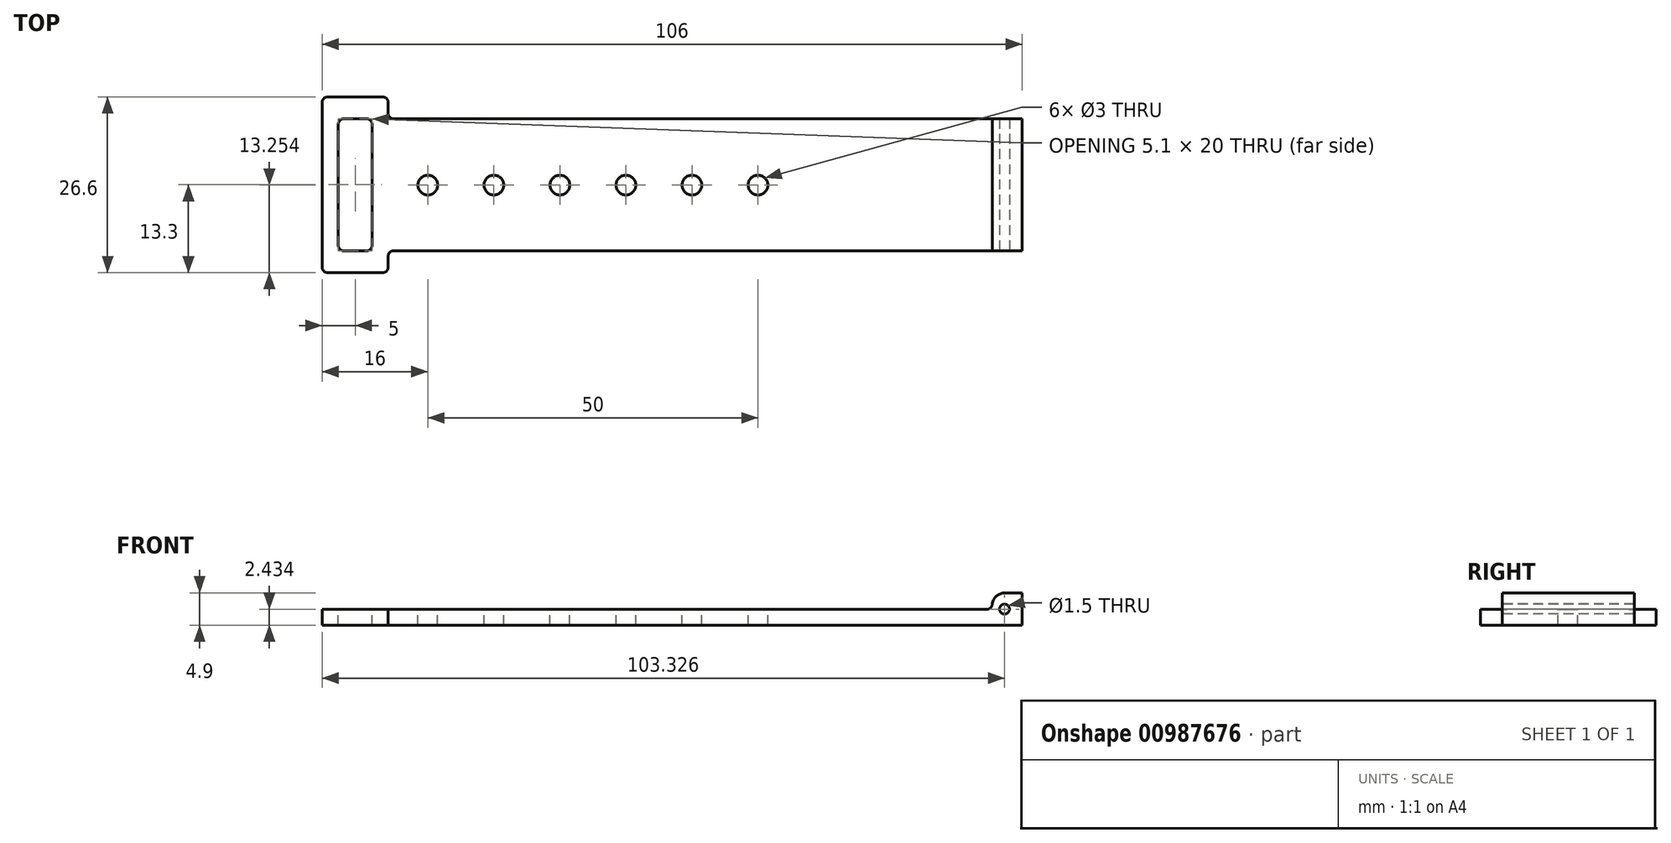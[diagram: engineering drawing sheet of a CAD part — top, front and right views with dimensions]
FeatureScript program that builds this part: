
annotation { "Feature Type Name" : "Feature", "Feature Type Description" : "" }
export const myFeature = defineFeature(function(context is Context, id is Id, definition is map)
    precondition{}
    {
        {
            var Q0;
            Q0=qCreatedBy(makeId("Top.planeOp"),FACE);
            var sketch = newSketch(context, id + "F0", { "sketchPlane" : qUnion([Q0])});
            skLineSegment(sketch, "E0", {"start": v(0, 0) * mm, "end": v(-96, 0) * mm});
            skLineSegment(sketch, "E1", {"start": v(-96, 20) * mm, "end": v(0, 20) * mm});
            skLineSegment(sketch, "E2", {"start": v(0, 20) * mm, "end": v(0, 0) * mm});
            skPoint(sketch, "E3.visualSharp", {"position": v(-100, 20) * mm});
            skPoint(sketch, "E4.visualSharp", {"position": v(-100, 0) * mm});
            skLineSegment(sketch, "E5", {"start": v(-96, 20) * mm, "end": v(-96, 0) * mm});
            skSolve(sketch);
        }
        {
            var Q0;
            Q0=makeQuery(id+"F0.imprint","IMPRINT",FACE,{"disambiguationData":[TD([[makeQuery(id+"F0.imprint","IMPRINT",EDGE,{"derivedFrom":sQuery(id+"F0.wireOp",EDGE,"E0")}),-1.0]])]});
            extrude(context, id + "F1", {"entities" : qUnion([Q0]), "depth" : 2.4 * mm, "offsetDistance" : 25 * mm});
        }
        {
            var Q0;
            Q0=makeQuery(id+"F1.opExtrude","CAP_FACE",FACE,{"disambiguationData":[OSD([sQuery(id+"F0.wireOp",EDGE,"E0"),sQuery(id+"F0.wireOp",EDGE,"AKXXqW1o-zOXN-sCXT-5YLg-LlBWR1qxFu5Y"),sQuery(id+"F0.wireOp",EDGE,"E1"),sQuery(id+"F0.wireOp",EDGE,"E2"),sQuery(id+"F0.wireOp",EDGE,"E3.filletArc"),sQuery(id+"F0.wireOp",EDGE,"E4.filletArc")])],"isStart":false});
            var sketch = newSketch(context, id + "F2", { "sketchPlane" : qUnion([Q0])});
            skLineSegment(sketch, "E6", {"start": v(0, 20) * mm, "end": v(-4, 20) * mm});
            skLineSegment(sketch, "E7", {"start": v(-4, 20) * mm, "end": v(-4, 0) * mm});
            skLineSegment(sketch, "E8", {"start": v(-4, 0) * mm, "end": v(0, 0) * mm});
            skLineSegment(sketch, "E9", {"start": v(0, 0) * mm, "end": v(0, 20) * mm});
            skLineSegment(sketch, "E10", {"start": v(-96, 20) * mm, "end": v(0, 0) * mm});
            skSolve(sketch);
        }
        {
            var Q0;
            Q0=makeQuery(id+"F1.opExtrude","SWEPT_FACE",FACE,{"disambiguationData":[OSD([sQuery(id+"F0.wireOp",EDGE,"E0")])]});
            var sketch = newSketch(context, id + "F3", { "sketchPlane" : qUnion([Q0])});
            skLineSegment(sketch, "E11", {"start": v(0, 2.4) * mm, "end": v(0, 4.9) * mm});
            skLineSegment(sketch, "E12", {"start": v(0, 4.9) * mm, "end": v(-2.56, 4.9) * mm});
            skLineSegment(sketch, "E13", {"start": v(-4.54, 2.4) * mm, "end": v(0, 2.4) * mm});
            skPoint(sketch, "E14.visualSharp", {"position": v(-4.54, 4.9) * mm});
            skArc(sketch, "E14.filletArc", {"start": v(-2.56, 4.9) * mm, "mid": v(-3.86, 4.42) * mm, "end": v(-4.54, 3.2) * mm});
            skLineSegment(sketch, "E15", {"start": v(-5.34, 2.4) * mm, "end": v(-5.73, 2.4) * mm});
            skPoint(sketch, "E16.visualSharp", {"position": v(-4.54, 2.4) * mm});
            skArc(sketch, "E16.filletArc", {"start": v(-5.34, 2.4) * mm, "mid": v(-4.77, 2.63) * mm, "end": v(-4.54, 3.2) * mm});
            skSolve(sketch);
        }
        {
            var Q0;
            Q0=makeQuery(id+"F3.imprint","IMPRINT",FACE,{"disambiguationData":[TD([[makeQuery(id+"F3.imprint","IMPRINT",EDGE,{"derivedFrom":sQuery(id+"F3.wireOp",EDGE,"E11")}),1.0]])]});
            extrude(context, id + "F4", {"entities" : qUnion([Q0]), "operationType" : NewBodyOperationType.ADD, "oppositeDirection" : true, "depth" : 20 * mm, "offsetDistance" : 25 * mm});
        }
        {
            var Q0;
            Q0=makeQuery(id+"F4.boolean.opBoolean","MERGE",FACE,{"derivedFrom":[makeQuery(id+"F1.opExtrude","SWEPT_FACE",FACE,{"disambiguationData":[OSD([sQuery(id+"F0.wireOp",EDGE,"E0")])]}),makeQuery(id+"F4.opExtrude","CAP_FACE",FACE,{"disambiguationData":[OSD([sQuery(id+"F3.wireOp",EDGE,"E11"),sQuery(id+"F3.wireOp",EDGE,"E12"),sQuery(id+"F3.wireOp",EDGE,"nSELvPSm-3Vxk-T1EU-R1aP-sd0dZwsSSjfP"),sQuery(id+"F3.wireOp",EDGE,"E14.filletArc"),sQuery(id+"F3.wireOp",EDGE,"E13")])],"isStart":true})]});
            var sketch = newSketch(context, id + "F5", { "sketchPlane" : qUnion([Q0])});
            skCircle(sketch, "E17", {"center": v(-2.67, 2.43) * mm, "radius": 0.75 * mm});
            skLineSegment(sketch, "E18", {"start": v(0, 4.9) * mm, "end": v(0, 2.43) * mm});
            skLineSegment(sketch, "E19", {"start": v(0, 2.43) * mm, "end": v(-2.67, 2.43) * mm});
            skSolve(sketch);
        }
        {
            var Q0;
            Q0=makeQuery(id+"F5.imprint","IMPRINT",FACE,{"disambiguationData":[TD([[makeQuery(id+"F5.imprint","IMPRINT",EDGE,{"derivedFrom":sQuery(id+"F5.wireOp",EDGE,"E17")}),1.0]])]});
            extrude(context, id + "F6", {"entities" : qUnion([Q0]), "operationType" : NewBodyOperationType.REMOVE, "endBound" : BoundingType.THROUGH_ALL, "oppositeDirection" : true, "depth" : 25 * mm, "offsetDistance" : 25 * mm});
        }
        {
            var Q0;
            {var subQ2=sQuery(id+"F2.wireOp",EDGE,"E7");Q0=makeQuery(id+"F2.imprint","IMPRINT",FACE,{"disambiguationData":[TD([[makeQuery(id+"F2.imprint","IMPRINT",EDGE,{"derivedFrom":subQ2}),-1.0]])]});}
            var sketch = newSketch(context, id + "F7", { "sketchPlane" : qUnion([Q0])});
            skLineSegment(sketch, "E20", {"start": v(-100, 9.95) * mm, "end": v(-90, 9.95) * mm});
            skCircle(sketch, "E21", {"center": v(-90, 9.95) * mm, "radius": 1.5 * mm});
            skCircle(sketch, "E22.1.0.0", {"center": v(-80, 9.95) * mm, "radius": 1.5 * mm});
            skCircle(sketch, "E22.2.0.0", {"center": v(-70, 9.95) * mm, "radius": 1.5 * mm});
            skCircle(sketch, "E22.3.0.0", {"center": v(-60, 9.95) * mm, "radius": 1.5 * mm});
            skCircle(sketch, "E22.4.0.0", {"center": v(-50, 9.95) * mm, "radius": 1.5 * mm});
            skCircle(sketch, "E22.5.0.0", {"center": v(-40, 9.95) * mm, "radius": 1.5 * mm});
            skLineSegment(sketch, "E22.direction1", {"start": v(-90, 9.95) * mm, "end": v(-80, 9.95) * mm, "construction": true});
            skSolve(sketch);
        }
        {
            var Q0;
            Q0 = qSketchRegion(id + "F7", true);
            extrude(context, id + "F8", {"entities" : qUnion([Q0]), "operationType" : NewBodyOperationType.REMOVE, "endBound" : BoundingType.THROUGH_ALL, "oppositeDirection" : true, "depth" : 25 * mm, "offsetDistance" : 25 * mm});
        }
        {
            var Q0;
            {var subQ2=sQuery(id+"F2.wireOp",EDGE,"E7");Q0=makeQuery(id+"F2.imprint","IMPRINT",FACE,{"disambiguationData":[TD([[makeQuery(id+"F2.imprint","IMPRINT",EDGE,{"derivedFrom":subQ2}),-1.0]])]});}
            var sketch = newSketch(context, id + "F9", { "sketchPlane" : qUnion([Q0])});
            skLineSegment(sketch, "E23", {"start": v(-6, 0) * mm, "end": v(-95.2, 0) * mm});
            skLineSegment(sketch, "E24", {"start": v(-96, 0) * mm, "end": v(-96, 20) * mm});
            skLineSegment(sketch, "E25", {"start": v(-96, 10) * mm, "end": v(-6, 10) * mm, "construction": true});
            skLineSegment(sketch, "E26", {"start": v(-6, 10) * mm, "end": v(-198.41, 10) * mm, "construction": true});
            skLineSegment(sketch, "E27", {"start": v(-96, 20.8) * mm, "end": v(-96, 22.5) * mm});
            skLineSegment(sketch, "E28", {"start": v(-96.8, 23.3) * mm, "end": v(-105.2, 23.3) * mm});
            skLineSegment(sketch, "E29", {"start": v(-106, 22.5) * mm, "end": v(-106, -2.5) * mm});
            skLineSegment(sketch, "E30", {"start": v(-106, -3.3) * mm, "end": v(-96, -3.3) * mm});
            skLineSegment(sketch, "E31", {"start": v(-96, -2.5) * mm, "end": v(-96, -0.8) * mm});
            skLineSegment(sketch, "E32", {"start": v(-95.2, 20) * mm, "end": v(-6, 20) * mm});
            skLineSegment(sketch, "E33", {"start": v(-6, 20) * mm, "end": v(-6, 0) * mm});
            skLineSegment(sketch, "E34", {"start": v(-105.2, -3.3) * mm, "end": v(-103.3, -3.3) * mm});
            skLineSegment(sketch, "E35", {"start": v(-96.8, -3.3) * mm, "end": v(-98.7, -3.3) * mm});
            skLineSegment(sketch, "E36", {"start": v(-102.75, 20) * mm, "end": v(-99.25, 20) * mm});
            skLineSegment(sketch, "E37", {"start": v(-98.45, 19.2) * mm, "end": v(-98.45, 0.8) * mm});
            skLineSegment(sketch, "E38", {"start": v(-99.25, 0) * mm, "end": v(-102.75, 0) * mm});
            skLineSegment(sketch, "E39", {"start": v(-103.55, 0.8) * mm, "end": v(-103.55, 19.2) * mm});
            skPoint(sketch, "E40.visualSharp", {"position": v(-103.55, 20) * mm});
            skArc(sketch, "E40.filletArc", {"start": v(-102.75, 20) * mm, "mid": v(-103.32, 19.77) * mm, "end": v(-103.55, 19.2) * mm});
            skPoint(sketch, "E41.visualSharp", {"position": v(-98.45, 20) * mm});
            skArc(sketch, "E41.filletArc", {"start": v(-98.45, 19.2) * mm, "mid": v(-98.68, 19.77) * mm, "end": v(-99.25, 20) * mm});
            skPoint(sketch, "E42.visualSharp", {"position": v(-98.45, 0) * mm});
            skArc(sketch, "E42.filletArc", {"start": v(-99.25, 0) * mm, "mid": v(-98.68, 0.23) * mm, "end": v(-98.45, 0.8) * mm});
            skPoint(sketch, "E43.visualSharp", {"position": v(-103.55, 0) * mm});
            skArc(sketch, "E43.filletArc", {"start": v(-103.55, 0.8) * mm, "mid": v(-103.32, 0.23) * mm, "end": v(-102.75, 0) * mm});
            skPoint(sketch, "E44.visualSharp", {"position": v(-106, 23.3) * mm});
            skArc(sketch, "E44.filletArc", {"start": v(-105.2, 23.3) * mm, "mid": v(-105.77, 23.07) * mm, "end": v(-106, 22.5) * mm});
            skPoint(sketch, "E45.visualSharp", {"position": v(-96, 23.3) * mm});
            skArc(sketch, "E45.filletArc", {"start": v(-96, 22.5) * mm, "mid": v(-96.23, 23.07) * mm, "end": v(-96.8, 23.3) * mm});
            skPoint(sketch, "E46.visualSharp", {"position": v(-96, -3.3) * mm});
            skArc(sketch, "E46.filletArc", {"start": v(-96.8, -3.3) * mm, "mid": v(-96.23, -3.07) * mm, "end": v(-96, -2.5) * mm});
            skPoint(sketch, "E47.visualSharp", {"position": v(-106, -3.3) * mm});
            skArc(sketch, "E47.filletArc", {"start": v(-106, -2.5) * mm, "mid": v(-105.77, -3.07) * mm, "end": v(-105.2, -3.3) * mm});
            skPoint(sketch, "E48.visualSharp", {"position": v(-96, 20) * mm});
            skArc(sketch, "E48.filletArc", {"start": v(-96, 20.8) * mm, "mid": v(-95.77, 20.23) * mm, "end": v(-95.2, 20) * mm});
            skPoint(sketch, "E49.visualSharp", {"position": v(-96, 0) * mm});
            skArc(sketch, "E49.filletArc", {"start": v(-95.2, 0) * mm, "mid": v(-95.77, -0.23) * mm, "end": v(-96, -0.8) * mm});
            skPoint(sketch, "E50", {"position": v(-101, 10) * mm});
            skPoint(sketch, "E50.positionSnap0", {"position": v(-103.55, 10) * mm});
            skPoint(sketch, "E50.positionSnap1", {"position": v(-101, 20) * mm});
            skPoint(sketch, "E51", {"position": v(-106, 10) * mm});
            skPoint(sketch, "E52.positionSnap0", {"position": v(-101, 23.3) * mm});
            skSolve(sketch);
        }
        {
            var Q0;
            Q0 = qSketchRegion(id + "F9", true);
            extrude(context, id + "F10", {"entities" : qUnion([Q0]), "operationType" : NewBodyOperationType.ADD, "oppositeDirection" : true, "depth" : 2.4 * mm, "offsetDistance" : 25 * mm});
        }
        {
            var Q0;
            Q0 = qSketchRegion(id + "F7", true);
            extrude(context, id + "F11", {"entities" : qUnion([Q0]), "operationType" : NewBodyOperationType.REMOVE, "endBound" : BoundingType.THROUGH_ALL, "oppositeDirection" : true, "depth" : 25 * mm, "offsetDistance" : 25 * mm});
        }
    });
